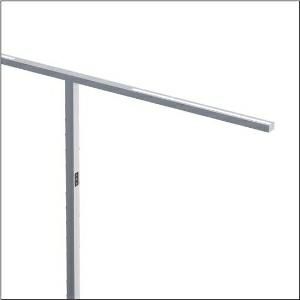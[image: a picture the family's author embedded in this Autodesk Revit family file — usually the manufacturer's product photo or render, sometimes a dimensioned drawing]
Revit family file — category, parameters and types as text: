
# Revit family: silica_31_floor_duo_51my52hmtcs
name_source: partatom
category: Lighting Fixtures
units: mm (PartAtom-declared; Revit-internal decimal feet)

## family parameters
Cut with Voids When Loaded = No
Host = Face
Light Source = No
Part Type = Normal
Room Calculation Point = No
Round Connector Dimension = Use Diameter
Shared = No

## types (1)
- --- (1 x LED, 17040 lm, 142 W, 4000K)
    Apparent Load = 142 VA
    CIE Flux Codes = 86 100 100 24 100
    Color Rendering = 80
    Color Temperature = 4000K
    Default Elevation = 1800 mm
    Description = Silica® 31 Floor duo, floorstanding luminaire, secondary optical cover: cover panel, of PMMA, light emission: direct/indirect distribution, primary light characteristic: symmetric, installation type: not mounted, LED, rated luminous flux: 17.040lm, luminous efficacy: 120lm/W, light colour: 8tw, colour temperature: 2700..6500K, control gear: Touchdim, daylight-dependent control, with cable with plug, mains connection: 230V, AC, 50Hz, connection cable included, cable length: 2,5m, rated input power: 142W, luminaire head, of aluminium, coated, metallic grey (RAL 9006), length: 2.372mm, width: 52mm, supporting column, angular, of aluminium, coated, silver, baseplate, of steel, coated, metallic grey (RAL 9006), local control - self-sufficient standalone sensors, direct and indirect component separately switchable, protection rating (complete): IP20, insulation class (complete): insulation class I (protective earthing), certification: CE, ENEC, permissible operating ambient temperature: -20..+40°C, standard: EN 50419, packaging unit: 1 piece
    Height = 36 mm
    Lamp = 1 x LED
    Lamp Light Flux = 17040 lm
    Lamp Power = 142 W
    Lamp count = 1
    Length = 2372 mm
    Luminous efficacy = 120 lm/W
    Manufacturer = Siteco
    ModVariant = No
    Model = 51MY52HMTCS
    Mounting Place = Floor
    Mounting Type = Freestanding
    Number of Poles = 1
    OnlyDefault = Yes
    Power Factor = 1
    Product Name = Silica 31 Floor duo
    Product group = floorstanding luminaire
    ProductGroupID = 1302
    Protection Class = Protection class I
    Protection Degree = IP 20
    RLX_Detail_Level = 1
    RLX_Emergency_Light_Flux = 0 lm
    RLX_Emergency_Type = 0
    RLX_Emergency_Type_DB = No
    RlxData = <blob elided: 17973 chars, md5=3b15d9ac>
    Socket = socket
    Standby Power = 0 W
    System Light Flux = 17040 lm
    System Power = 142 W
    Type Comments = factory setting
    Type Image = l_1275342.jpg
    URL = http://relux.com
    VarID = @adj_087097
    Voltage = 0 V
    Weight = 0.00 kg
    Width = 52 mm  [stored 0.170604 ft]

note: [stored X ft] marks values corroborated as IEEE doubles in the binary element streams (Revit-internal decimal feet)

## geometry (parser evidence)
native form markers: Blend x4, Sweep x14
no freeform markers — native parametric forms only
